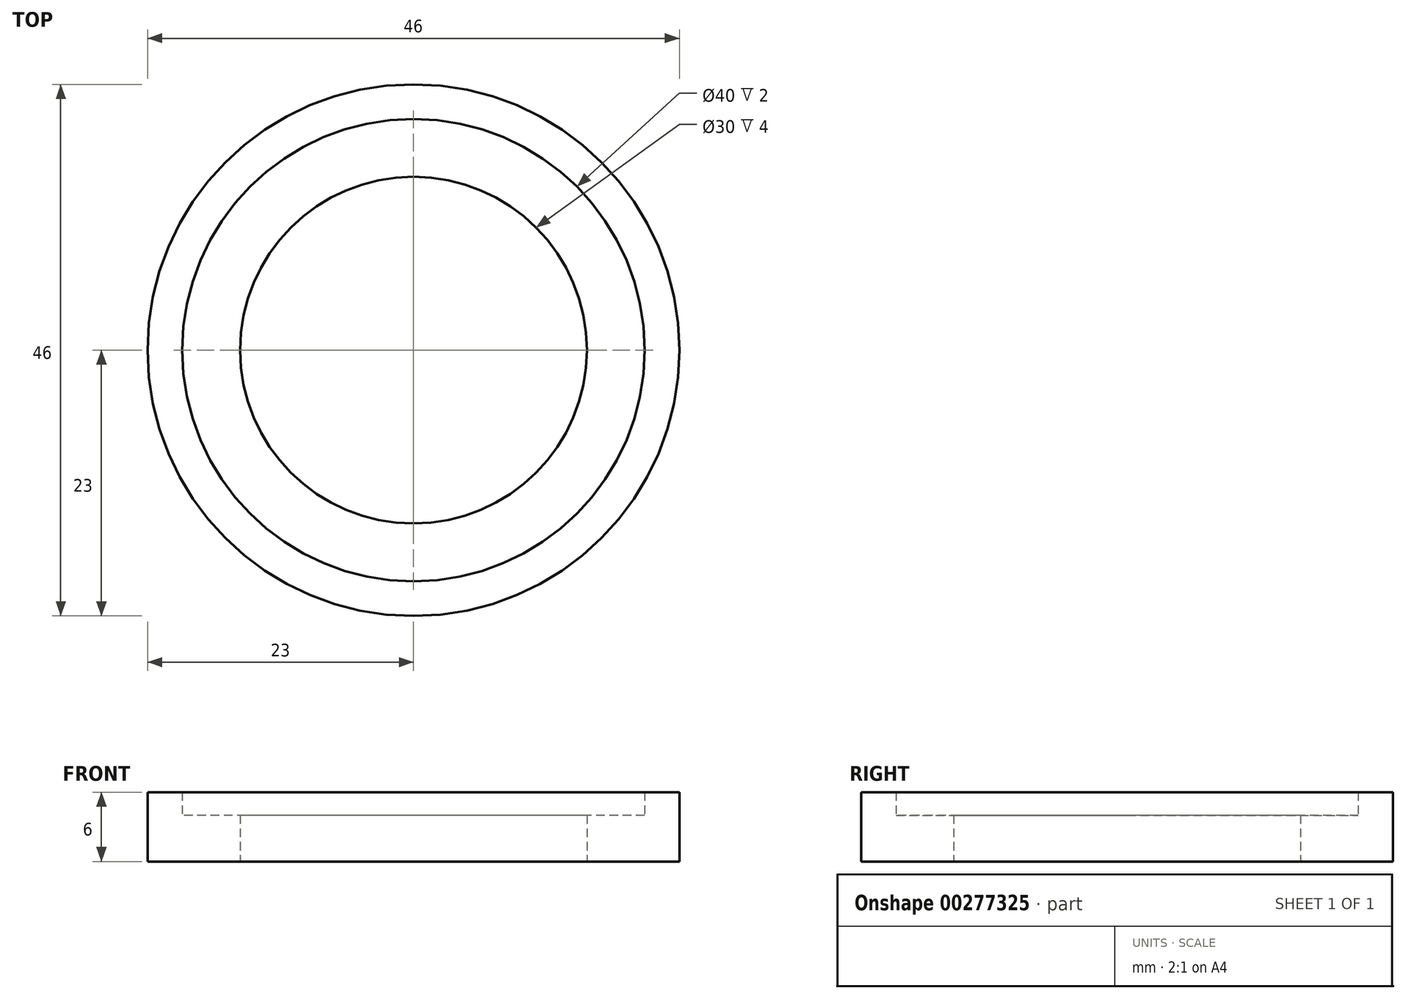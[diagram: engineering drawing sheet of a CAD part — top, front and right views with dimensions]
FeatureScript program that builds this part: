
annotation { "Feature Type Name" : "Feature", "Feature Type Description" : "" }
export const myFeature = defineFeature(function(context is Context, id is Id, definition is map)
    precondition{}
    {
        {
            var Q0;
            Q0=qCreatedBy(makeId("Top.planeOp"),FACE);
            var sketch = newSketch(context, id + "F0", { "sketchPlane" : qUnion([Q0])});
            skCircle(sketch, "E0", {"center": v(0, 0) * mm, "radius": 23 * mm});
            skCircle(sketch, "E1", {"center": v(0, 0) * mm, "radius": 15 * mm});
            skCircle(sketch, "E2", {"center": v(0, 0) * mm, "radius": 20 * mm});
            skSolve(sketch);
        }
        {
            var Q0;
            Q0=qSketchRegion(id+"F0",true);
            extrude(context, id + "F1", {"entities" : qUnion([Q0]), "depth" : 6 * mm});
        }
        {
            var Q0;
            Q0=makeQuery(id+"F0.imprint","IMPRINT",FACE,{"disambiguationData":[TD([[makeQuery(id+"F0.imprint","IMPRINT",EDGE,{"derivedFrom":sQuery(id+"F0.wireOp",EDGE,"E1")}),-1.0]])]});
            extrude(context, id + "F2", {"entities" : qUnion([Q0]), "operationType" : NewBodyOperationType.ADD, "depth" : 4 * mm});
        }
    });
